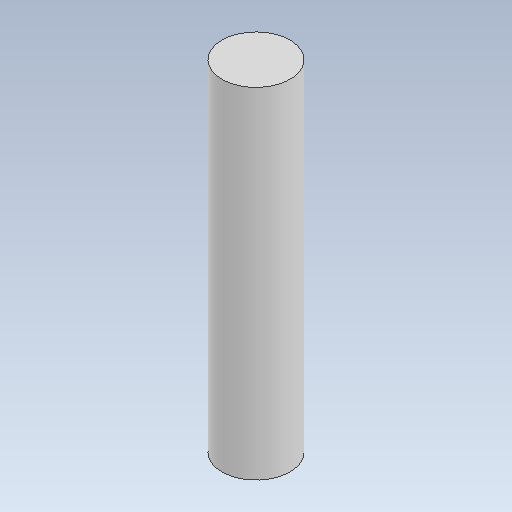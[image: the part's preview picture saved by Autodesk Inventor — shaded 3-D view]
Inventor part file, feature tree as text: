
AUTODESK INVENTOR PART (.ipt)
format: ipt  version: 2020 (Build 240168000, 168)  size: 75,264 bytes
history: native  units: mm
features: extrude x1, sketch x1
ambient origin geometry x8: Origin, YZ Plane, XZ Plane, XY Plane, X Axis, Y Axis, Z Axis, Center Point
bodies: Solid1 (feature_tree)
feature tree (2):
  extrude  "Extrusion1"  Depth=15.0mm TaperAngle=0.0deg
  sketch  "Sketch1"  dims[d0=3.0mm d1=15.0mm d2=0.0mm]
